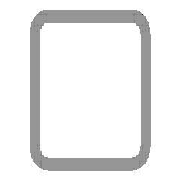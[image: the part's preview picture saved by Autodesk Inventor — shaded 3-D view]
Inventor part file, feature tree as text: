
AUTODESK INVENTOR PART (.ipt)
format: ipt  version: 2025 (Build 290162010, 162A)  size: 135,168 bytes
history: native  units: mm (DEFAULTED — no unit token found)
features: other x4, sketch x1, plane x1
ambient origin geometry x8: Origin, YZ Plane, XZ Plane, XY Plane, X Axis, Y Axis, Z Axis, Center Point
bodies: Solid1 (feature_tree), Body (feature_tree)
feature tree (6):
  parser-record x1  (decoder bookkeeping rows leaked as tree rows — omitted from the tree; the rows remain in map.json)
  other  "Driven Length"
  other  "Start plane"
  other  "End plane"
  sketch  "Sketch3"  dims[d3=2209.072203mm d4=0.0mm d7=6.0mm d9=80.0mm d11=80.0mm d12=3.0mm d13=-0.0mm d14=2209.072203mm d15=40.0mm d16=40.0mm d17=90.0deg d18=2209.072203mm]
  plane  "Work Plane3"
